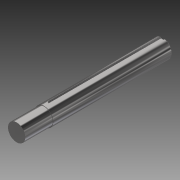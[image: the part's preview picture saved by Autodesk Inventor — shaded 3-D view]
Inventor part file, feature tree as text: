
AUTODESK INVENTOR PART (.ipt)
format: ipt  version: 2013 (Build 170138000, 138)  size: 110,080 bytes
history: native  units: in
note: dims shown in document units (in); Inventor stores cm internally (conversion verified against a paired STEP export)
features: extrude x4, sketch x3, fillet x1, chamfer x1, thread x1
ambient origin geometry x8: Origin, YZ Plane, XZ Plane, XY Plane, X Axis, Y Axis, Z Axis, Center Point
bodies: Solid1 (feature_tree)
feature tree (10):
  sketch  "Sketch1"  dims[d0=0.5in d2=0.185in]
  extrude  "Extrusion1"  Depth=0.185in
  extrude  "Extrusion2"  Depth=0.5in TaperAngle=0.0deg
  extrude  "Extrusion3"  Depth=0.75in TaperAngle=0.0deg
  extrude  "Extrusion4"  Depth=0.125in
  fillet  "Fillet1"  Radius=0.0625in
  chamfer  "Chamfer1"  Distance=3.125in
  thread  "Thread1"  [1 undecoded]
  sketch  "Sketch2"  dims[d3=3.25in d4=0.0in d5=0.5in d6=0.0in]
  sketch  "Sketch3"  dims[d7=0.4724in d9=0.75in d10=0.0in d11=0.125in d13=0.0625in d14=3.125in d15=0.0in d16=0.0625in d17=0.025in d18=0.125in d19=45.0deg d20=1.0in d21=0.0in]
note: 1 required parameter value undecoded (feature->parameter linkage not recoverable at this tier; creation-order binding heuristic only, values carry confidence <= 0.55)
